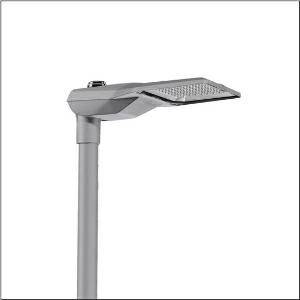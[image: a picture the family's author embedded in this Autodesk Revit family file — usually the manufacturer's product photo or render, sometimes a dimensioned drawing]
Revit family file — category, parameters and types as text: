
# Revit family: streetlight_sl_21_midi___stw1_0a_5xe7e47n08nb_2a9b
name_source: partatom
category: Lighting Fixtures
units: mm (PartAtom-declared; Revit-internal decimal feet)

## family parameters
Cut with Voids When Loaded = No
Host = Face
Light Source = No
Part Type = Normal
Room Calculation Point = No
Round Connector Dimension = Use Diameter
Shared = No

## types (1)
- --- (1 x LED, 23710 lm, 151.2 W, 4000K)
    Apparent Load = 151 VA
    CIE Flux Codes = 39 75 98 100 100
    Color Rendering = 70
    Color Temperature = 4000K
    Default Elevation = 1800 mm
    Description = Streetlight SL 21 midi, mast luminaire, primary light control with lens, of PMMA, primary optical cover: cover, of toughened safety glass, transparent, light distribution: STW1.0a, light emission: direct distribution, primary light characteristic: asymmetric, installation type: side-entry, LED, 3G 2.5mm², High Power LED, rated luminous flux: 23.710lm, luminous efficacy: 157lm/W, light colour: 740, colour temperature: 4000K, control: overheat protection, presetting dimming linear, constant luminous flux control, time-dependent luminous flux control, flexible luminous flux parameterisation, mains connection: 220..240V, AC, 50/60Hz, connection cable pre-assembled, cable length: 12,5m, wiring characteristics: H05VV-F, start of lifetime: 151W, end of service life: 157W, reduction: 70W, luminaire housing, of diecast aluminium (EN AC-44300), powder-coated, Siteco® metallic grey (DB 702S), corrosivity category C5 mid according to DIN EN ISO 12944, multi-level sealing system, sealing non-destructively replaceable, inclination adjustable: 0°, 5°, 10°, 15°, length: 644mm, width: 335mm, height: 110mm, spigot size: 42mm (side-entry), protection rating (complete): IP66, insulation class (complete): insulation class I (protective earthing), certification: CE, ENEC, ENEC+, VDE, impact resistance: IK09, permissible operating ambient temperature for outdoor applications: -40..+50°C, standard-compliant lighting for roads and squares, packaging unit: 1 piece

Light Distribution: STW1.0a
    Height = 111 mm
    Lamp = 1 x LED
    Lamp Light Flux = 23710 lm
    Lamp Power = 151.2 W
    Lamp count = 1
    Length = 644 mm
    Luminous efficacy = 157 lm/W
    Manufacturer = Siteco
    ModVariant = No
    Model = 5XE7E47N08NB
    Number of Poles = 1
    OnlyDefault = Yes
    Power Factor = 1
    Product Name = Streetlight SL 21 midi | STW1.0a
    Product group = mast luminaire | pylon top
    ProductGroupID = 6100
    Protection Class = Protection class I
    Protection Degree = IP 66
    RLX_Detail_Level = 1
    RLX_Emergency_Light_Flux = 0 lm
    RLX_Emergency_Type = 0
    RLX_Emergency_Type_DB = No
    RlxData = <blob elided: 90517 chars, md5=846aaa58>
    Socket = socket
    Standby Power = 0 W
    System Light Flux = 23710 lm
    System Power = 151 W
    Type Comments = factory setting: luminous flux: 100 % | dim-lin: 254 | 802 mA
    Type Image = l_1294377.jpg
    URL = http://relux.com
    VarID = @adj_084273
    Voltage = 0 V
    Weight = 0.00 kg
    Width = 336 mm

## geometry (parser evidence)
native form markers: Blend x4, Sweep x10
no freeform markers — native parametric forms only
